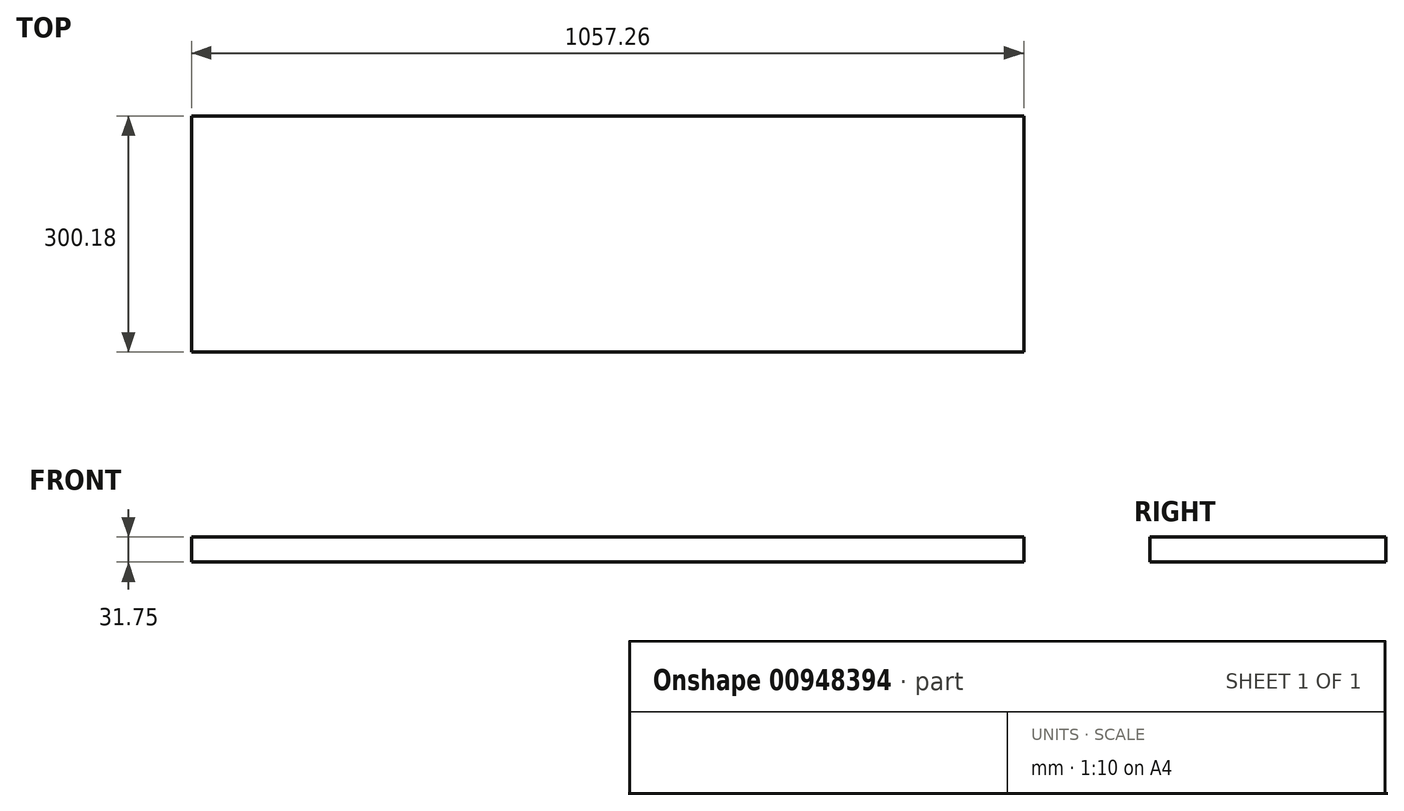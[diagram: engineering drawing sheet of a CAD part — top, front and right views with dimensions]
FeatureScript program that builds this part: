
annotation { "Feature Type Name" : "Feature", "Feature Type Description" : "" }
export const myFeature = defineFeature(function(context is Context, id is Id, definition is map)
    precondition{}
    {
        {
            var Q0;
            Q0=qCreatedBy(makeId("Top.planeOp"),FACE);
            var sketch = newSketch(context, id + "F0", { "sketchPlane" : qUnion([Q0])});
            skLineSegment(sketch, "E0.bottom", {"start": v(-528.63, 150.09) * mm, "end": v(528.63, 150.09) * mm});
            skLineSegment(sketch, "E0.top", {"start": v(-528.63, -150.09) * mm, "end": v(528.63, -150.09) * mm});
            skLineSegment(sketch, "E0.left", {"start": v(-528.63, 150.09) * mm, "end": v(-528.63, -150.09) * mm});
            skLineSegment(sketch, "E0.right", {"start": v(528.63, 150.09) * mm, "end": v(528.63, -150.09) * mm});
            skSolve(sketch);
        }
        {
            var Q0;
            Q0=makeQuery(id+"F0.imprint","IMPRINT",FACE,{"disambiguationData":[TD([[makeQuery(id+"F0.imprint","IMPRINT",EDGE,{"derivedFrom":sQuery(id+"F0.wireOp",EDGE,"E0.bottom")}),-1.0]])]});
            extrude(context, id + "F1", {"entities" : qUnion([Q0]), "depth" : 31.75 * mm, "offsetDistance" : 25.4 * mm});
        }
    });
